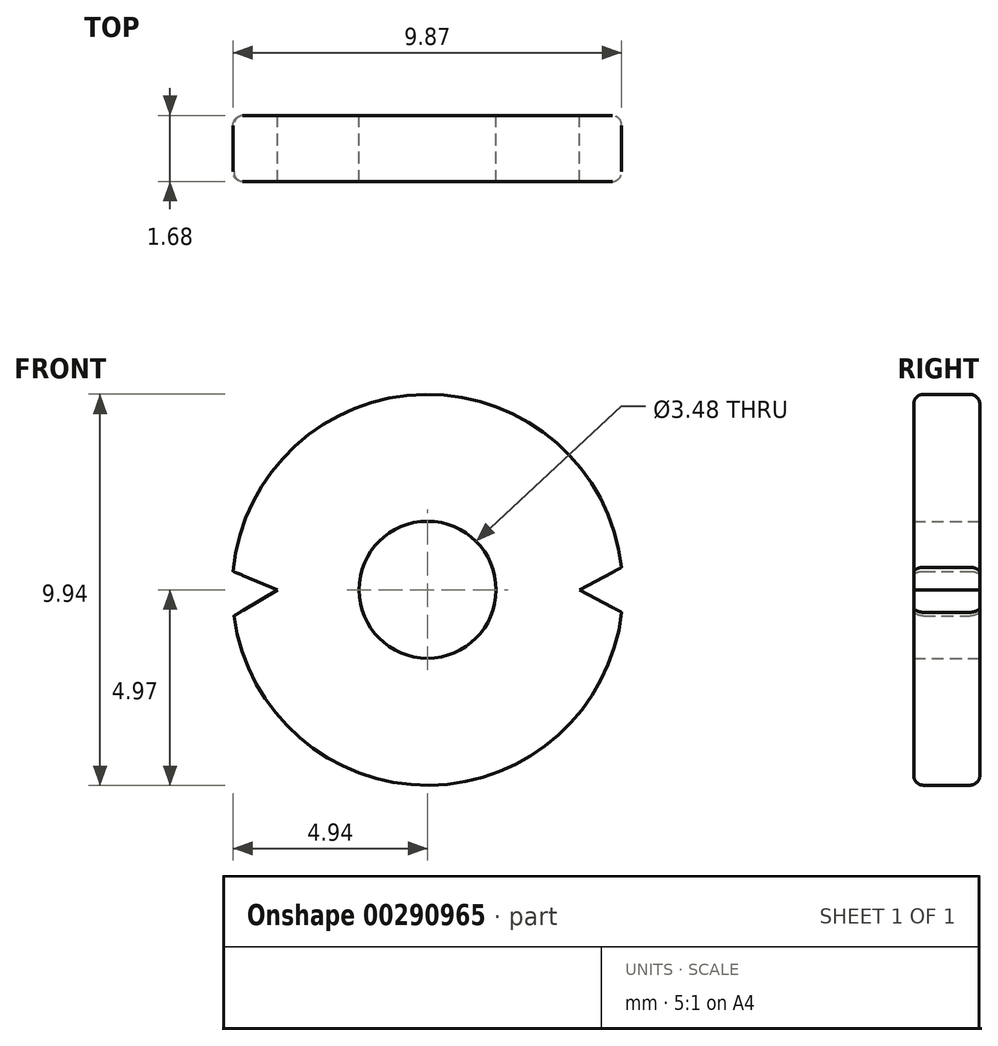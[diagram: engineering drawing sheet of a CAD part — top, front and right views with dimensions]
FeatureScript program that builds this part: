
annotation { "Feature Type Name" : "Feature", "Feature Type Description" : "" }
export const myFeature = defineFeature(function(context is Context, id is Id, definition is map)
    precondition{}
    {
        {
            var Q0;
            Q0=qCreatedBy(makeId("Front.planeOp"),FACE);
            var sketch = newSketch(context, id + "F0", { "sketchPlane" : qUnion([Q0])});
            skCircle(sketch, "E0", {"center": v(0, 0) * mm, "radius": 4.97 * mm});
            skCircle(sketch, "E1", {"center": v(0, 0) * mm, "radius": 1.74 * mm});
            skLineSegment(sketch, "E2", {"start": v(-3.8, 0) * mm, "end": v(-4.96, 0.48) * mm});
            skLineSegment(sketch, "E3", {"start": v(-3.8, 0) * mm, "end": v(-4.92, -0.66) * mm});
            skLineSegment(sketch, "E4", {"start": v(4.93, -0.57) * mm, "end": v(3.86, 0) * mm});
            skLineSegment(sketch, "E5", {"start": v(3.86, 0) * mm, "end": v(4.93, 0.57) * mm});
            skSolve(sketch);
        }
        {
            var Q0;
            Q0=makeQuery(id+"F0.imprint","IMPRINT",FACE,{"disambiguationData":[TD([[makeQuery(id+"F0.imprint","IMPRINT",EDGE,{"derivedFrom":sQuery(id+"F0.wireOp",EDGE,"E0")}),1.0]])]});
            var Q1;
            Q1=sQuery(id+"F0.wireOp",EDGE,"E0");
            extrude(context, id + "F1", {"entities" : qUnion([Q0]), "surfaceEntities" : qUnion([Q1]), "endBound" : BoundingType.SYMMETRIC, "depth" : 1.68 * mm});
        }
        {
            var Q0;
            Q0=makeQuery(id+"F1.opExtrude","CAP_EDGE",EDGE,{"disambiguationData":[OSD([sQuery(id+"F0.wireOp",EDGE,"E0")])],"isStart":false});
            var Q1;
            Q1=makeQuery(id+"F1.opExtrude","CAP_EDGE",EDGE,{"disambiguationData":[OSD([sQuery(id+"F0.wireOp",EDGE,"E0")])],"isStart":true});
            fillet(context, id + "F2", {"entities" : qUnion([Q0, Q1]), "radius" : .25 * mm, "tangentPropagation" : true, "allowEdgeOverflow" : false});
        }
    });
